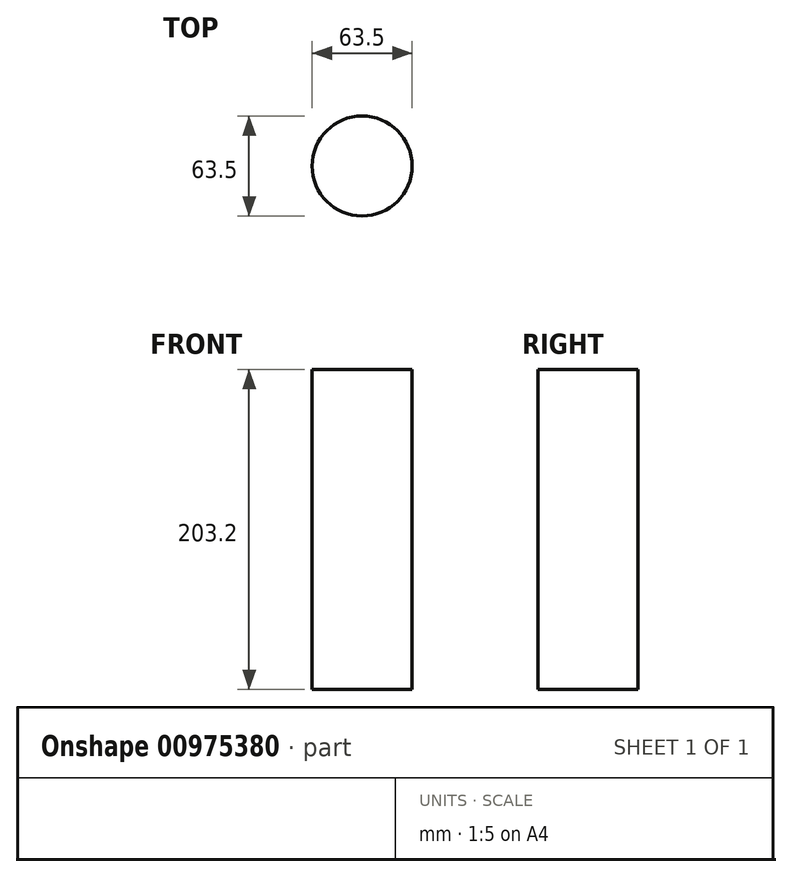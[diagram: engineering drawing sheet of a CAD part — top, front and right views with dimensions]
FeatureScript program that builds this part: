
annotation { "Feature Type Name" : "Feature", "Feature Type Description" : "" }
export const myFeature = defineFeature(function(context is Context, id is Id, definition is map)
    precondition{}
    {
        {
            var Q0;
            Q0=qCreatedBy(makeId("Top.planeOp"),FACE);
            var Q1;
            Q1=qCreatedBy(makeId("Top.planeOp"),FACE);
            var sketch = newSketch(context, id + "F0", { "sketchPlane" : qUnion([Q0, Q1])});
            skCircle(sketch, "E0", {"center": v(0, 0) * mm, "radius": 31.75 * mm});
            skSolve(sketch);
        }
        {
            var Q0;
            Q0=makeQuery(id+"F0.imprint","IMPRINT",FACE,{"disambiguationData":[TD([[makeQuery(id+"F0.imprint","IMPRINT",EDGE,{"derivedFrom":sQuery(id+"F0.wireOp",EDGE,"E0")}),1.0]])]});
            var Q1;
            Q1=makeQuery(id+"F0.imprint","IMPRINT",FACE,{"disambiguationData":[TD([[makeQuery(id+"F0.imprint","IMPRINT",EDGE,{"derivedFrom":sQuery(id+"F0.wireOp",EDGE,"E0")}),1.0]])]});
            extrude(context, id + "F1", {"entities" : qUnion([Q0, Q1]), "endBound" : BoundingType.SYMMETRIC, "depth" : 203.2 * mm, "offsetDistance" : 25.4 * mm});
        }
    });
